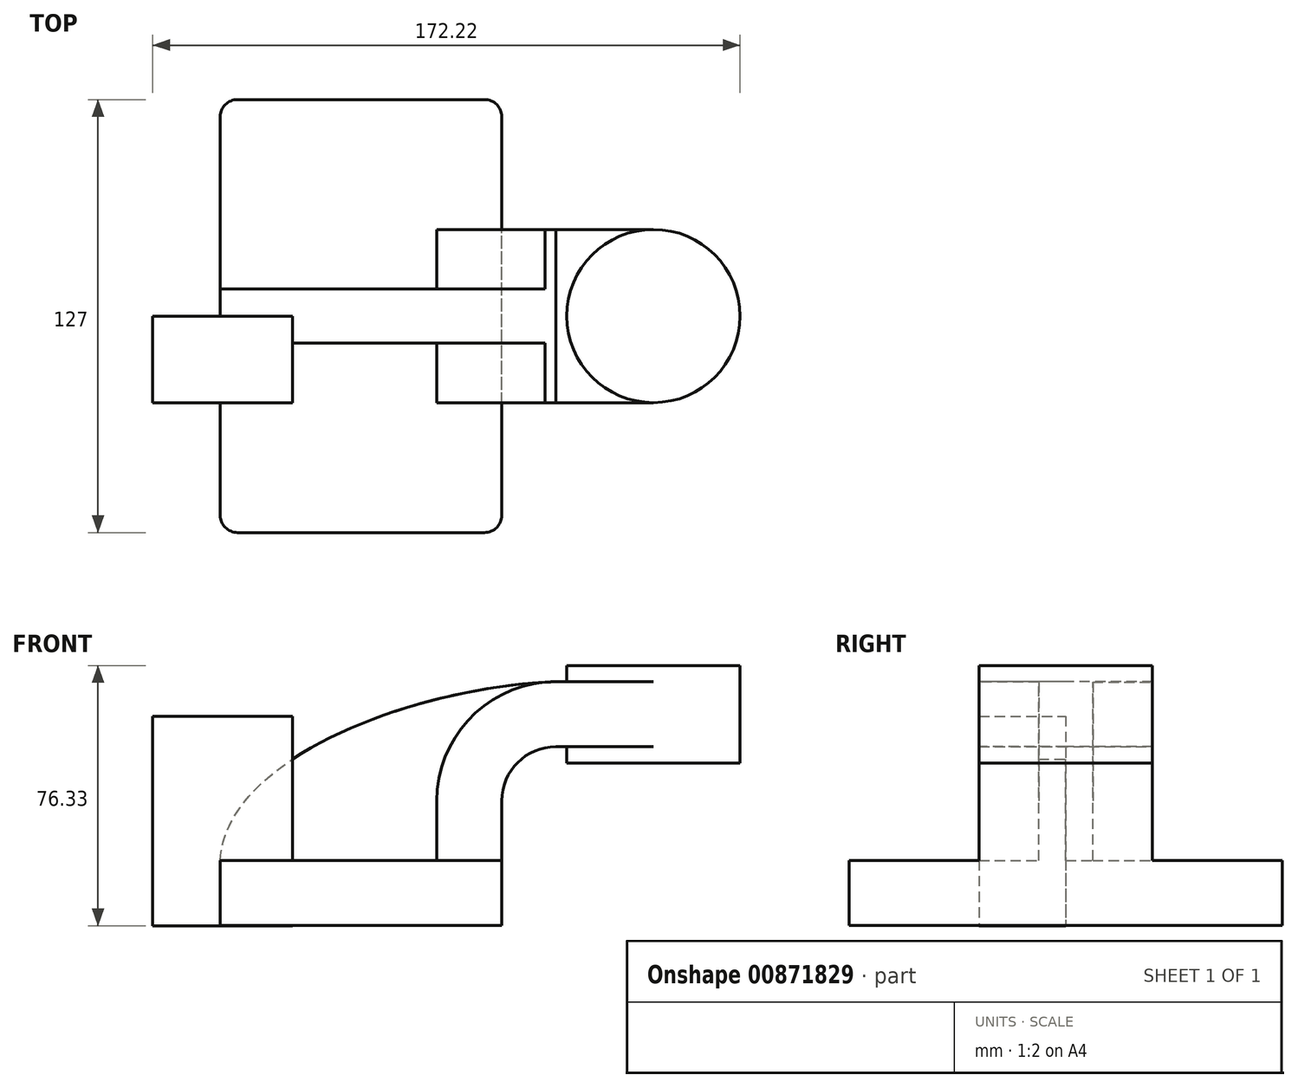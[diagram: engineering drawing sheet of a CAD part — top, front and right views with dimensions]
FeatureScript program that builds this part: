
annotation { "Feature Type Name" : "Feature", "Feature Type Description" : "" }
export const myFeature = defineFeature(function(context is Context, id is Id, definition is map)
    precondition{}
    {
        {
            var Q0;
            Q0=qCreatedBy(makeId("Front.planeOp"),FACE);
            var sketch = newSketch(context, id + "F0", { "sketchPlane" : qUnion([Q0])});
            skLineSegment(sketch, "E0.rect.bottom", {"start": v(-41.28, 9.52) * mm, "end": v(41.28, 9.52) * mm});
            skLineSegment(sketch, "E0.rect.top", {"start": v(-41.28, -9.52) * mm, "end": v(41.28, -9.52) * mm});
            skLineSegment(sketch, "E0.rect.left", {"start": v(-41.28, 9.52) * mm, "end": v(-41.28, -9.52) * mm});
            skLineSegment(sketch, "E0.rect.right", {"start": v(41.28, 9.52) * mm, "end": v(41.28, -9.52) * mm});
            skPoint(sketch, "E0.rect.middle", {"position": v(0, 0) * mm});
            skLineSegment(sketch, "E1", {"start": v(41.28, 9.52) * mm, "end": v(41.28, 27) * mm});
            skArc(sketch, "E2", {"start": v(41.28, 27) * mm, "mid": v(45.92, 38.23) * mm, "end": v(57.15, 42.88) * mm});
            skLineSegment(sketch, "E3", {"start": v(57.15, 42.88) * mm, "end": v(85.72, 42.88) * mm});
            skLineSegment(sketch, "E4.rect.bottom", {"start": v(60.32, 38.1) * mm, "end": v(111.12, 38.1) * mm});
            skLineSegment(sketch, "E4.rect.top", {"start": v(60.32, 66.68) * mm, "end": v(111.12, 66.68) * mm});
            skLineSegment(sketch, "E4.rect.left", {"start": v(60.32, 38.1) * mm, "end": v(60.32, 66.68) * mm});
            skLineSegment(sketch, "E4.rect.right", {"start": v(111.13, 38.1) * mm, "end": v(111.12, 66.68) * mm});
            skPoint(sketch, "E4.rect.middle", {"position": v(85.72, 52.39) * mm});
            skLineSegment(sketch, "E5.0", {"start": v(57.15, 61.93) * mm, "end": v(85.72, 61.93) * mm});
            skArc(sketch, "E5.1", {"start": v(22.23, 27) * mm, "mid": v(32.45, 51.7) * mm, "end": v(57.15, 61.93) * mm});
            skLineSegment(sketch, "E5.2", {"start": v(22.23, 9.52) * mm, "end": v(22.23, 27) * mm});
            skLineSegment(sketch, "E6", {"start": v(85.72, 38.1) * mm, "end": v(85.72, 66.68) * mm});
            skFitSpline(sketch, "E7", {"points": [v(-41.28, 9.53) * mm, v(57.15, 61.93) * mm], "startDerivative": vector(5.2, 92.34) * mm, "endDerivative": vector(120.92, 4.22) * mm});
            skSolve(sketch);
        }
        {
            var Q0;
            Q0=makeQuery(id+"F0.imprint","IMPRINT",FACE,{"disambiguationData":[TD([[makeQuery(id+"F0.imprint","IMPRINT",EDGE,{"derivedFrom":sQuery(id+"F0.wireOp",EDGE,"E0.rect.top")}),1.0]])]});
            extrude(context, id + "F1", {"entities" : qUnion([Q0]), "endBound" : BoundingType.SYMMETRIC, "depth" : 127 * mm});
        }
        {
            var Q0;
            {var subQ9=sQuery(id+"F0.wireOp",EDGE,"E1");Q0=makeQuery(id+"F0.imprint","IMPRINT",FACE,{"disambiguationData":[TD([[makeQuery(id+"F0.imprint","IMPRINT",EDGE,{"derivedFrom":subQ9}),1.0]])]});}
            var Q1;
            {var subQ0=sQuery(id+"F0.wireOp",EDGE,"E6");var subQ1=sQuery(id+"F0.wireOp",EDGE,"E3");var subQ2=makeQuery(id+"F0.imprint","INTERSECT",VERTEX,{"derivedFrom":[subQ1,subQ0]});Q1=makeQuery(id+"F0.imprint","IMPRINT",FACE,{"disambiguationData":[TD([[makeQuery(id+"F0.imprint","IMPRINT",EDGE,{"disambiguationData":[TD([[subQ2,1.0]])],"derivedFrom":subQ1}),1.0]])]});}
            extrude(context, id + "F2", {"entities" : qUnion([Q0, Q1]), "operationType" : NewBodyOperationType.ADD, "endBound" : BoundingType.SYMMETRIC, "depth" : 50.8 * mm});
        }
        {
            var Q0;
            {var subQ3=sQuery(id+"F0.wireOp",EDGE,"E5.2");Q0=makeQuery(id+"F0.imprint","IMPRINT",FACE,{"disambiguationData":[TD([[makeQuery(id+"F0.imprint","IMPRINT",EDGE,{"derivedFrom":subQ3}),1.0]])]});}
            extrude(context, id + "F3", {"entities" : qUnion([Q0]), "operationType" : NewBodyOperationType.ADD, "endBound" : BoundingType.SYMMETRIC, "depth" : 15.88 * mm});
        }
        {
            var Q0;
            {var subQ5=sQuery(id+"F0.wireOp",EDGE,"E4.rect.right");Q0=makeQuery(id+"F0.imprint","IMPRINT",FACE,{"disambiguationData":[TD([[makeQuery(id+"F0.imprint","IMPRINT",EDGE,{"derivedFrom":subQ5}),1.0]])]});}
            var Q1;
            Q1=sQuery(id+"F0.wireOp",EDGE,"E6");
            revolve(context, id + "F4", {"operationType" : NewBodyOperationType.ADD, "entities" : qUnion([Q0]), "axis" : qUnion([Q1]), "revolveType" : RevolveType.FULL});
        }
        {
            var Q0;
            Q0=makeQuery(id+"F1.opExtrude","CAP_EDGE",EDGE,{"disambiguationData":[OSD([sQuery(id+"F0.wireOp",EDGE,"E0.rect.right")])],"isStart":false});
            var Q1;
            Q1=makeQuery(id+"F1.opExtrude","CAP_EDGE",EDGE,{"disambiguationData":[OSD([sQuery(id+"F0.wireOp",EDGE,"E0.rect.left")])],"isStart":false});
            var Q2;
            Q2=makeQuery(id+"F1.opExtrude","CAP_EDGE",EDGE,{"disambiguationData":[OSD([sQuery(id+"F0.wireOp",EDGE,"E0.rect.right")])],"isStart":true});
            var Q3;
            Q3=makeQuery(id+"F1.opExtrude","CAP_EDGE",EDGE,{"disambiguationData":[OSD([sQuery(id+"F0.wireOp",EDGE,"E0.rect.left")])],"isStart":true});
            fillet(context, id + "F5", {"entities" : qUnion([Q0, Q1, Q2, Q3]), "radius" : 5.08 * mm, "tangentPropagation" : true, "allowEdgeOverflow" : false});
        }
        {
            var Q0;
            Q0=qCreatedBy(makeId("Front.planeOp"),FACE);
            var sketch = newSketch(context, id + "F6", { "sketchPlane" : qUnion([Q0])});
            skLineSegment(sketch, "E8.bottom", {"start": v(-61.1, 51.82) * mm, "end": v(-20.11, 51.82) * mm});
            skLineSegment(sketch, "E8.top", {"start": v(-61.1, -9.65) * mm, "end": v(-20.11, -9.65) * mm});
            skLineSegment(sketch, "E8.left", {"start": v(-61.1, 51.82) * mm, "end": v(-61.1, -9.65) * mm});
            skLineSegment(sketch, "E8.right", {"start": v(-20.11, 51.82) * mm, "end": v(-20.11, -9.65) * mm});
            skSolve(sketch);
        }
        {
            var Q0;
            Q0 = qSketchRegion(id + "F6", true);
            extrude(context, id + "F7", {"entities" : qUnion([Q0]), "operationType" : NewBodyOperationType.ADD, "depth" : 25.4 * mm, "offsetDistance" : 25.4 * mm});
        }
    });
